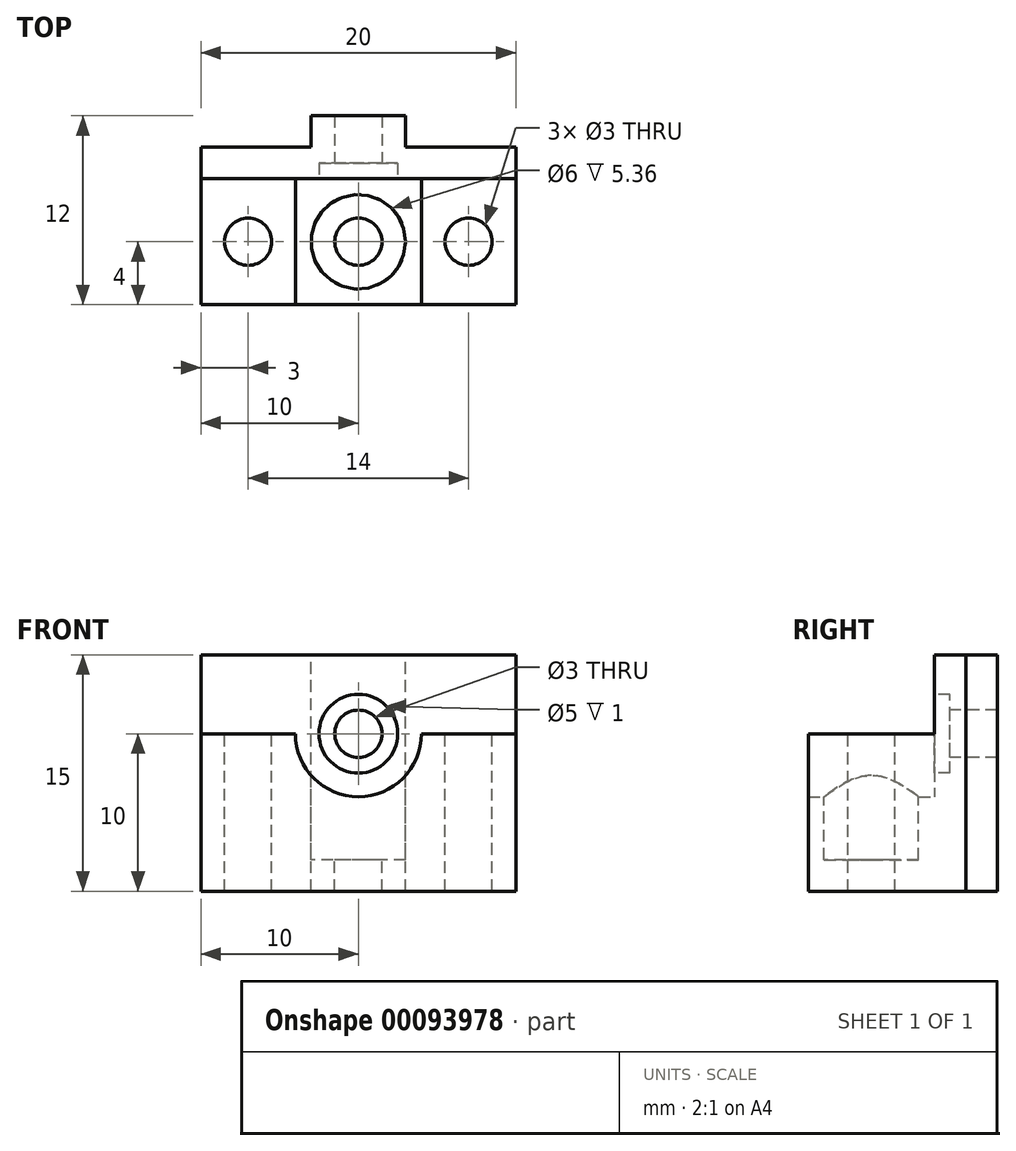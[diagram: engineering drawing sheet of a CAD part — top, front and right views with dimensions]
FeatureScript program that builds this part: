
annotation { "Feature Type Name" : "Feature", "Feature Type Description" : "" }
export const myFeature = defineFeature(function(context is Context, id is Id, definition is map)
    precondition{}
    {
        {
            var Q0;
            Q0=qCreatedBy(makeId("Top.planeOp"),FACE);
            var sketch = newSketch(context, id + "F0", { "sketchPlane" : qUnion([Q0])});
            skLineSegment(sketch, "E0.bottom", {"start": v(10, 5) * mm, "end": v(3, 5) * mm});
            skLineSegment(sketch, "E0.top", {"start": v(10, -5) * mm, "end": v(-10, -5) * mm});
            skLineSegment(sketch, "E0.left", {"start": v(10, 5) * mm, "end": v(10, -5) * mm});
            skLineSegment(sketch, "E0.right", {"start": v(-10, 5) * mm, "end": v(-10, -5) * mm});
            skPoint(sketch, "E0.middle", {"position": v(0, 0) * mm});
            skLineSegment(sketch, "E1", {"start": v(-3, 5) * mm, "end": v(-3, 7) * mm});
            skLineSegment(sketch, "E2", {"start": v(-3, 7) * mm, "end": v(3, 7) * mm});
            skLineSegment(sketch, "E3", {"start": v(3, 7) * mm, "end": v(3, 5) * mm});
            skPoint(sketch, "E4", {"position": v(0, 7) * mm});
            skLineSegment(sketch, "E5.trimOffspring", {"start": v(-3, 5) * mm, "end": v(-10, 5) * mm});
            skLineSegment(sketch, "E6", {"start": v(0, -5) * mm, "end": v(0, 3) * mm});
            skLineSegment(sketch, "E7", {"start": v(0, 3) * mm, "end": v(4, 3) * mm});
            skLineSegment(sketch, "E8", {"start": v(4, 3) * mm, "end": v(4, -5) * mm});
            skCircle(sketch, "E9", {"center": v(7, -1) * mm, "radius": 1.5 * mm});
            skCircle(sketch, "E10.MirrorC", {"center": v(-7, -1) * mm, "radius": 1.5 * mm});
            skCircle(sketch, "E11", {"center": v(0, -1) * mm, "radius": 1.5 * mm});
            skCircle(sketch, "E12", {"center": v(0, -1) * mm, "radius": 3 * mm});
            skSolve(sketch);
        }
        {
            var Q0;
            Q0=makeQuery(id+"F0.imprint","IMPRINT",FACE,{"disambiguationData":[TD([[makeQuery(id+"F0.imprint","IMPRINT",EDGE,{"derivedFrom":sQuery(id+"F0.wireOp",EDGE,"E0.bottom")}),1.0]])]});
            var Q1;
            {var subQ0=sQuery(id+"F0.wireOp",EDGE,"E7");Q1=makeQuery(id+"F0.imprint","IMPRINT",FACE,{"disambiguationData":[TD([[makeQuery(id+"F0.imprint","IMPRINT",EDGE,{"derivedFrom":subQ0}),-1.0]])]});}
            var Q2;
            {var subQ0=sQuery(id+"F0.wireOp",EDGE,"E12");var subQ1=sQuery(id+"F0.wireOp",EDGE,"E6");var subQ2=makeQuery(id+"F0.imprint","INTERSECT",VERTEX,{"disambiguationData":[OD(0.0)],"derivedFrom":[subQ1,subQ0]});Q2=makeQuery(id+"F0.imprint","IMPRINT",FACE,{"disambiguationData":[TD([[makeQuery(id+"F0.imprint","IMPRINT",EDGE,{"disambiguationData":[TD([[subQ2,-1.0]])],"derivedFrom":subQ1}),-1.0]])]});}
            var Q3;
            {var subQ0=sQuery(id+"F0.wireOp",EDGE,"E12");var subQ1=sQuery(id+"F0.wireOp",EDGE,"E6");var subQ2=makeQuery(id+"F0.imprint","INTERSECT",VERTEX,{"disambiguationData":[OD(0.0)],"derivedFrom":[subQ1,subQ0]});Q3=makeQuery(id+"F0.imprint","IMPRINT",FACE,{"disambiguationData":[TD([[makeQuery(id+"F0.imprint","IMPRINT",EDGE,{"disambiguationData":[TD([[subQ2,-1.0]])],"derivedFrom":subQ1}),1.0]])]});}
            extrude(context, id + "F1", {"entities" : qUnion([Q0, Q1, Q2, Q3]), "oppositeDirection" : true, "depth" : 10 * mm});
        }
        {
            var Q0;
            {var subQ0=sQuery(id+"F0.wireOp",EDGE,"E7");Q0=makeQuery(id+"F0.imprint","IMPRINT",FACE,{"disambiguationData":[TD([[makeQuery(id+"F0.imprint","IMPRINT",EDGE,{"derivedFrom":subQ0}),-1.0]])]});}
            var Q1;
            {var subQ0=sQuery(id+"F0.wireOp",EDGE,"E12");var subQ1=sQuery(id+"F0.wireOp",EDGE,"E6");var subQ2=makeQuery(id+"F0.imprint","INTERSECT",VERTEX,{"disambiguationData":[OD(0.0)],"derivedFrom":[subQ1,subQ0]});Q1=makeQuery(id+"F0.imprint","IMPRINT",FACE,{"disambiguationData":[TD([[makeQuery(id+"F0.imprint","IMPRINT",EDGE,{"disambiguationData":[TD([[subQ2,-1.0]])],"derivedFrom":subQ1}),-1.0]])]});}
            var Q2;
            Q2=sQuery(id+"F0.wireOp",EDGE,"E6");
            revolve(context, id + "F2", {"operationType" : NewBodyOperationType.REMOVE, "entities" : qUnion([Q0, Q1]), "axis" : qUnion([Q2]), "revolveType" : RevolveType.FULL, "oppositeDirection" : true});
        }
        {
            var Q0;
            {var subQ0=sQuery(id+"F0.wireOp",EDGE,"E12");var subQ1=sQuery(id+"F0.wireOp",EDGE,"E6");var subQ2=makeQuery(id+"F0.imprint","INTERSECT",VERTEX,{"disambiguationData":[OD(0.0)],"derivedFrom":[subQ1,subQ0]});Q0=makeQuery(id+"F0.imprint","IMPRINT",FACE,{"disambiguationData":[TD([[makeQuery(id+"F0.imprint","IMPRINT",EDGE,{"disambiguationData":[TD([[subQ2,-1.0]])],"derivedFrom":subQ1}),1.0]])]});}
            var Q1;
            {var subQ0=sQuery(id+"F0.wireOp",EDGE,"E12");var subQ1=sQuery(id+"F0.wireOp",EDGE,"E6");var subQ2=makeQuery(id+"F0.imprint","INTERSECT",VERTEX,{"disambiguationData":[OD(0.0)],"derivedFrom":[subQ1,subQ0]});Q1=makeQuery(id+"F0.imprint","IMPRINT",FACE,{"disambiguationData":[TD([[makeQuery(id+"F0.imprint","IMPRINT",EDGE,{"disambiguationData":[TD([[subQ2,-1.0]])],"derivedFrom":subQ1}),-1.0]])]});}
            extrude(context, id + "F3", {"entities" : qUnion([Q0, Q1]), "operationType" : NewBodyOperationType.REMOVE, "oppositeDirection" : true, "depth" : 8 * mm});
        }
        {
            var Q0;
            Q0=makeQuery(id+"F0.imprint","IMPRINT",FACE,{"disambiguationData":[TD([[makeQuery(id+"F0.imprint","IMPRINT",EDGE,{"derivedFrom":sQuery(id+"F0.wireOp",EDGE,"E0.bottom")}),1.0]])]});
            var sketch = newSketch(context, id + "F4", { "sketchPlane" : qUnion([Q0])});
            skLineSegment(sketch, "E13", {"start": v(-10, 3) * mm, "end": v(10, 3) * mm});
            skSolve(sketch);
        }
        {
            var Q0;
            {var subQ0=makeQuery(id+"F0.imprint","IMPRINT",EDGE,{"derivedFrom":sQuery(id+"F0.wireOp",EDGE,"E0.bottom")});Q0=makeQuery(id+"F4.imprint","IMPRINT",FACE,{"disambiguationData":[TD([[makeQuery(id+"F4.imprint","IMPRINT",EDGE,{"derivedFrom":subQ0}),1.0]])]});}
            extrude(context, id + "F5", {"entities" : qUnion([Q0]), "operationType" : NewBodyOperationType.ADD, "depth" : 5 * mm});
        }
        {
            var Q0;
            Q0=makeQuery(id+"F5.boolean.opBoolean","MERGE",FACE,{"derivedFrom":[makeQuery(id+"F2.boolean.opBoolean","COPY",FACE,{"derivedFrom":makeQuery(id+"F2.opRevolve","SWEPT_FACE",FACE,{"disambiguationData":[OSD([sQuery(id+"F0.wireOp",EDGE,"E7")])]})}),makeQuery(id+"F5.opExtrude","SWEPT_FACE",FACE,{"disambiguationData":[OSD([sQuery(id+"F4.wireOp",EDGE,"E13")])]})]});
            var sketch = newSketch(context, id + "F6", { "sketchPlane" : qUnion([Q0])});
            skCircle(sketch, "E14", {"center": v(0, 0) * mm, "radius": 1.5 * mm});
            skCircle(sketch, "E15", {"center": v(0, 0) * mm, "radius": 2.5 * mm});
            skSolve(sketch);
        }
        {
            var Q0;
            Q0=makeQuery(id+"F6.imprint","IMPRINT",FACE,{"disambiguationData":[TD([[makeQuery(id+"F6.imprint","IMPRINT",EDGE,{"derivedFrom":sQuery(id+"F6.wireOp",EDGE,"E14")}),1.0]])]});
            extrude(context, id + "F7", {"entities" : qUnion([Q0]), "operationType" : NewBodyOperationType.REMOVE, "endBound" : BoundingType.THROUGH_ALL, "oppositeDirection" : true, "depth" : 25 * mm});
        }
        {
            var Q0;
            Q0=makeQuery(id+"F6.imprint","IMPRINT",FACE,{"disambiguationData":[TD([[makeQuery(id+"F6.imprint","IMPRINT",EDGE,{"derivedFrom":sQuery(id+"F6.wireOp",EDGE,"E14")}),-1.0]])]});
            extrude(context, id + "F8", {"entities" : qUnion([Q0]), "operationType" : NewBodyOperationType.REMOVE, "oppositeDirection" : true, "depth" : 1 * mm});
        }
    });
